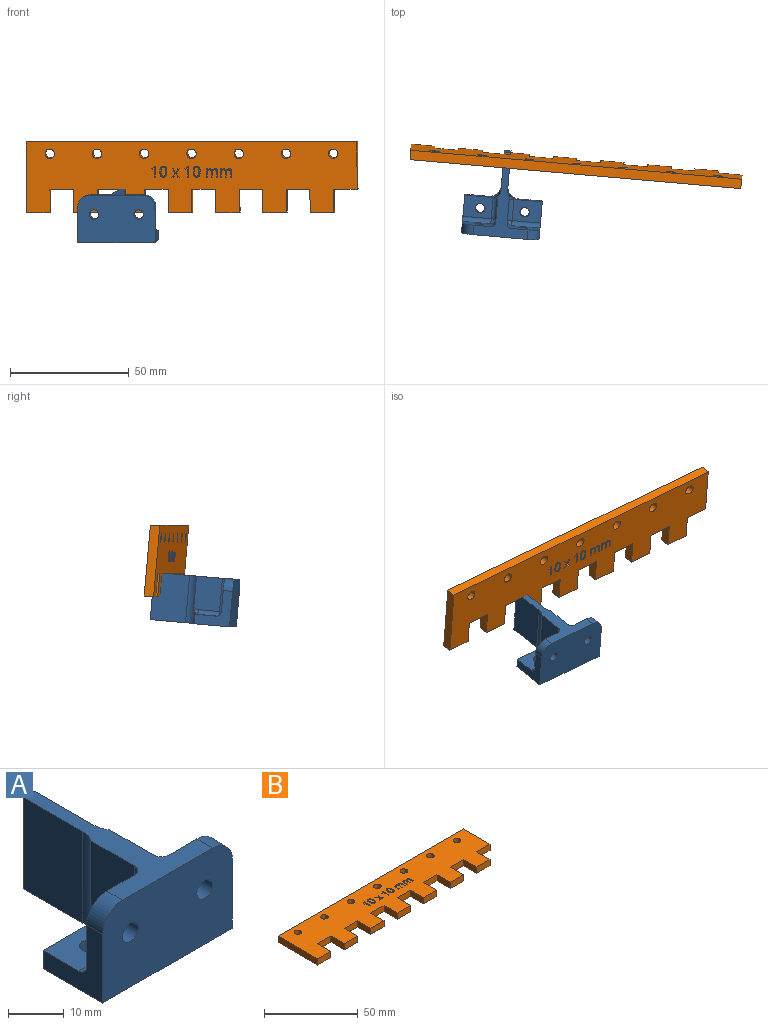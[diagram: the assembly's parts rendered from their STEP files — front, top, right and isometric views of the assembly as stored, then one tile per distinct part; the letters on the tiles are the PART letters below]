
ASSEMBLY  parts=2 mates=3
PART A: 36 faces, bbox 32.8x35x20 mm
  f0: plane 32.8x20mm, normal (0,-1,0), area 620.1mm2, adj f1,f10,f12,f13,f24,f25,f26,f27
  f1: plane 15x15mm, normal (1,0,0), area 104.9mm2, adj f0,f2,f13,f14,f15,f16,f27
  f2: plane 10x4mm, normal (0,1,0), area 40mm2, adj f1,f3,f13,f16
  f3: cylinder r=5mm len=20mm, axis (0,0,-1), area 84.6mm2, adj f2,f4,f12,f13,f17,f18,f28
  f4: plane 20x15mm, normal (1,0,0), area 300mm2, adj f3,f5,f12,f13
  f5: plane 20x2.8mm, normal (0,1,0), area 56mm2, adj f4,f6,f12,f13
  f6: plane 20x15mm, normal (-1,0,0), area 300mm2, adj f5,f7,f12,f13
  f7: cylinder r=5mm len=20mm, axis (0,0,-1), area 84.6mm2, adj f6,f8,f12,f13,f21,f23,f35
  f8: plane 10x4mm, normal (0,1,0), area 40mm2, adj f7,f10,f13,f22
  f9: cylinder r=2mm len=4mm, axis (0,0,-1), area 50.3mm2, adj f13,f22
  f10: plane 15x15mm, normal (-1,0,0), area 104.9mm2, adj f0,f8,f13,f19,f20,f22,f26
  f11: cylinder r=2mm len=4mm, axis (0,0,-1), area 50.3mm2, adj f13,f16
  f12: plane 35x22.8mm, normal (0,0,1), area 207.6mm2, adj f0,f3,f4,f5,f6,f7,f14,f18
  f13: plane 35x32.8mm, normal (0,0,-1), area 533.6mm2, adj f0,f1,f2,f3,f4,f5,f6,f7
  f14: plane 14x12mm, normal (0,1,0), area 150.1mm2, adj f1,f12,f15,f25,f27,f29
  f15: cylinder r=2mm len=12mm, axis (1,0,0), area 37.7mm2, adj f1,f14,f16,f31
  f16: plane 12x9mm, normal (0,0,1), area 95.4mm2, adj f1,f2,f11,f15,f17,f30
  f17: cylinder r=5mm len=2mm, axis (1,0,0), area 0.3mm2, adj f3,f16,f28
  f18: plane 14x11mm, normal (1,0,0), area 153.5mm2, adj f3,f12,f28,f29,f30
  f19: cylinder r=2mm len=12mm, axis (-1,0,0), area 37.7mm2, adj f10,f20,f22,f33
  f20: plane 14x12mm, normal (0,1,0), area 150.1mm2, adj f10,f12,f19,f24,f26,f32
  f21: cylinder r=5mm len=2mm, axis (-1,0,0), area 0.3mm2, adj f7,f22,f35
  f22: plane 12x9mm, normal (0,0,1), area 95.4mm2, adj f8,f9,f10,f19,f21,f34
  f23: plane 14x11mm, normal (-1,0,0), area 153.5mm2, adj f7,f12,f32,f34,f35
  f24: cylinder r=2mm len=4mm, axis (0,-1,0), area 50.3mm2, adj f0,f20
  f25: cylinder r=2mm len=4mm, axis (0,-1,0), area 50.3mm2, adj f0,f14
  f26: cylinder r=5mm len=5mm, axis (0,1,0), area 31.4mm2, adj f0,f10,f12,f20
  f27: cylinder r=5mm len=5mm, axis (0,-1,0), area 31.4mm2, adj f0,f1,f12,f14
  f28: torus R=3mm, axis (1,0,0), area 4.3mm2, adj f3,f17,f18,f30
  f29: cylinder r=2mm len=14mm, axis (0,0,-1), area 44mm2, adj f12,f14,f18,f31
  f30: cylinder r=2mm len=9mm, axis (0,1,0), area 28.3mm2, adj f16,f18,f28,f31
  f31: sphere r=2mm, area 6.3mm2, adj f15,f29,f30
  f32: cylinder r=2mm len=14mm, axis (0,0,1), area 44mm2, adj f12,f20,f23,f33
  f33: sphere r=2mm, area 6.3mm2, adj f19,f32,f34
  f34: cylinder r=2mm len=9mm, axis (0,-1,0), area 28.3mm2, adj f22,f23,f33,f35
  f35: torus R=3mm, axis (-1,0,0), area 4.3mm2, adj f7,f21,f23,f34
PART B: 166 faces, bbox 140x30x4 mm
  f0: plane 140x30mm, normal (0,0,1), area 3365.2mm2, adj f1,f2,f3,f4,f5,f6,f7,f8
  f1: plane 10x4mm, normal (-1,0,0), area 40mm2, adj f0,f2,f30,f31
  f2: plane 10x4mm, normal (0,-1,0), area 40mm2, adj f0,f1,f3,f31
  f3: plane 10x4mm, normal (1,0,0), area 40mm2, adj f0,f2,f4,f31
  f4: plane 10x4mm, normal (0,-1,0), area 40mm2, adj f0,f3,f5,f31
  f5: plane 10x4mm, normal (-1,0,0), area 40mm2, adj f0,f4,f6,f31
  f6: plane 10x4mm, normal (0,-1,0), area 40mm2, adj f0,f5,f7,f31
  f7: plane 10x4mm, normal (1,0,0), area 40mm2, adj f0,f6,f8,f31
  f8: plane 10x4mm, normal (0,-1,0), area 40mm2, adj f0,f7,f9,f31
  f9: plane 10x4mm, normal (-1,0,0), area 40mm2, adj f0,f8,f10,f31
  f10: plane 10x4mm, normal (0,-1,0), area 40mm2, adj f0,f9,f11,f31
  f11: plane 10x4mm, normal (1,0,0), area 40mm2, adj f0,f10,f12,f31
  f12: plane 10x4mm, normal (0,-1,0), area 40mm2, adj f0,f11,f13,f31
  f13: plane 10x4mm, normal (-1,0,0), area 40mm2, adj f0,f12,f14,f31
  f14: plane 10x4mm, normal (0,-1,0), area 40mm2, adj f0,f13,f15,f31
  f15: plane 10x4mm, normal (1,0,0), area 40mm2, adj f0,f14,f16,f31
  f16: plane 10x4mm, normal (0,-1,0), area 40mm2, adj f0,f15,f17,f31
  f17: plane 20x4mm, normal (1,0,0), area 80mm2, adj f0,f16,f18,f31
  f18: plane 140x4mm, normal (0,1,0), area 560mm2, adj f0,f17,f19,f31
  f19: plane 30x4mm, normal (-1,0,0), area 120mm2, adj f0,f18,f20,f31
  f20: plane 10x4mm, normal (0,-1,0), area 40mm2, adj f0,f19,f21,f31
  f21: plane 10x4mm, normal (1,0,0), area 40mm2, adj f0,f20,f22,f31
  f22: plane 10x4mm, normal (0,-1,0), area 40mm2, adj f0,f21,f23,f31
  f23: plane 10x4mm, normal (-1,0,0), area 40mm2, adj f0,f22,f24,f31
  f24: plane 10x4mm, normal (0,-1,0), area 40mm2, adj f0,f23,f25,f31
  f25: plane 10x4mm, normal (1,0,0), area 40mm2, adj f0,f24,f26,f31
  f26: plane 10x4mm, normal (0,-1,0), area 40mm2, adj f0,f25,f27,f31
  f27: plane 10x4mm, normal (-1,0,0), area 40mm2, adj f0,f26,f28,f31
  f28: plane 10x4mm, normal (0,-1,0), area 40mm2, adj f0,f27,f29,f31
  f29: plane 10x4mm, normal (1,0,0), area 40mm2, adj f0,f28,f30,f31
  f30: plane 10x4mm, normal (0,-1,0), area 40mm2, adj f0,f1,f29,f31
  f31: plane 140x30mm, normal (0,0,-1), area 3412mm2, adj f1,f2,f3,f4,f5,f6,f7,f8
  f32: cylinder r=2mm len=4mm, axis (0,0,1), area 50.3mm2, adj f0,f31
  f33: cylinder r=2mm len=4mm, axis (0,0,1), area 50.3mm2, adj f0,f31
  f34: cylinder r=2mm len=4mm, axis (0,0,1), area 50.3mm2, adj f0,f31
  f35: cylinder r=2mm len=4mm, axis (0,0,1), area 50.3mm2, adj f0,f31
  f36: cylinder r=2mm len=4mm, axis (0,0,1), area 50.3mm2, adj f0,f31
  f37: cylinder r=2mm len=4mm, axis (0,0,1), area 50.3mm2, adj f0,f31
  f38: cylinder r=2mm len=4mm, axis (0,0,1), area 50.3mm2, adj f0,f31
  f39: plane 2x1.68mm, normal (0.81,0.58,0), area 4.1mm2, adj f0,f40,f50,f51
  f40: plane 2x1.76mm, normal (0.81,-0.58,0), area 4.3mm2, adj f0,f39,f41,f51
  f41: plane 2x0.59mm, normal (0,1,0), area 1.2mm2, adj f0,f40,f42,f51
  f42: plane 2x1.4mm, normal (-0.82,0.57,0), area 3.4mm2, adj f0,f41,f43,f51
  f43: plane 2x1.4mm, normal (0.82,0.57,0), area 3.4mm2, adj f0,f42,f44,f51
  f44: plane 2x0.59mm, normal (0,1,0), area 1.2mm2, adj f0,f43,f45,f51
  f45: plane 2x1.76mm, normal (-0.81,-0.58,0), area 4.3mm2, adj f0,f44,f46,f51
  f46: plane 2x1.68mm, normal (-0.81,0.58,0), area 4.1mm2, adj f0,f45,f47,f51
  f47: plane 2x0.59mm, normal (0,-1,0), area 1.2mm2, adj f0,f46,f48,f51
  f48: plane 2x1.32mm, normal (0.82,-0.57,0), area 3.2mm2, adj f0,f47,f49,f51
  f49: plane 2x1.32mm, normal (-0.82,-0.57,0), area 3.2mm2, adj f0,f48,f50,f51
  f50: plane 2x0.59mm, normal (0,-1,0), area 1.2mm2, adj f0,f39,f49,f51
  f51: plane 3.44x3.12mm, normal (0,0,1), area 3.7mm2, adj f39,f40,f41,f42,f43,f44,f45,f46
  f52: plane 2x0.51mm, normal (0,1,0), area 1mm2, adj f0,f53,f60,f61
  f53: plane 4.59x2mm, normal (-1,0,0), area 9.2mm2, adj f0,f52,f54,f61
  f54: plane 2x0.44mm, normal (0,-1,0), area 0.9mm2, adj f0,f53,f55,f61
  f55: plane 2x1.22mm, normal (0.61,-0.79,0), area 3.1mm2, adj f0,f54,f56,f61
  f56: plane 2x0.36mm, normal (0.79,0.61,0), area 0.9mm2, adj f0,f55,f57,f61
  f57: extruded ~2x0.75mm, area 1.9mm2, adj f0,f56,f58,f61
  f58: extruded ~2x0.15mm, area 0.4mm2, adj f0,f57,f59,f61
  f59: extruded ~2x0.77mm, area 1.5mm2, adj f0,f58,f60,f61
  f60: plane 3.27x2mm, normal (1,0,0), area 6.5mm2, adj f0,f52,f59,f61
  f61: plane 4.59x1.65mm, normal (0,0,1), area 2.9mm2, adj f52,f53,f54,f55,f56,f57,f58,f59
  f62: plane 2.24x2mm, normal (1,0,0), area 4.5mm2, adj f0,f63,f89,f90
  f63: plane 2x0.52mm, normal (0,1,0), area 1mm2, adj f0,f62,f64,f90
  f64: plane 2.25x2mm, normal (-1,0,0), area 4.5mm2, adj f0,f63,f65,f90
  f65: extruded ~2x0.96mm, area 2.1mm2, adj f0,f64,f66,f90
  f66: extruded ~2x0.87mm, area 1.9mm2, adj f0,f65,f67,f90
  f67: extruded ~2x0.67mm, area 1.4mm2, adj f0,f66,f68,f90
  f68: extruded ~2x0.45mm, area 1.3mm2, adj f0,f67,f69,f90
  f69: plane 2x0.03mm, normal (0,-1,0), area 0.1mm2, adj f0,f68,f70,f90
  f70: extruded ~2x1.06mm, area 2.6mm2, adj f0,f69,f71,f90
  f71: extruded ~2x0.6mm, area 1.2mm2, adj f0,f70,f72,f90
  f72: extruded ~2x0.42mm, area 1.2mm2, adj f0,f71,f73,f90
  f73: plane 2x0.03mm, normal (0,-1,0), area 0.1mm2, adj f0,f72,f74,f90
  f74: plane 2x0.47mm, normal (-0.98,-0.18,0), area 1mm2, adj f0,f73,f75,f90
  f75: plane 2x0.42mm, normal (0,-1,0), area 0.8mm2, adj f0,f74,f76,f90
  f76: plane 3.44x2mm, normal (1,0,0), area 6.9mm2, adj f0,f75,f77,f90
  f77: plane 2x0.52mm, normal (0,1,0), area 1mm2, adj f0,f76,f78,f90
  f78: plane 2x1.81mm, normal (-1,0,0), area 3.6mm2, adj f0,f77,f79,f90
  f79: extruded ~2x0.96mm, area 2mm2, adj f0,f78,f80,f90
  f80: extruded ~2x0.72mm, area 1.6mm2, adj f0,f79,f81,f90
  f81: extruded ~2x0.55mm, area 1.2mm2, adj f0,f80,f82,f90
  f82: extruded ~2x0.62mm, area 1.3mm2, adj f0,f81,f83,f90
  f83: plane 2.24x2mm, normal (1,0,0), area 4.5mm2, adj f0,f82,f84,f90
  f84: plane 2x0.52mm, normal (0,1,0), area 1mm2, adj f0,f83,f85,f90
  f85: plane 2x1.92mm, normal (-1,0,0), area 3.8mm2, adj f0,f84,f86,f90
  f86: extruded ~2x0.86mm, area 1.8mm2, adj f0,f85,f87,f90
  f87: extruded ~2x0.72mm, area 1.6mm2, adj f0,f86,f88,f90
  f88: extruded ~2x0.55mm, area 1.2mm2, adj f0,f87,f89,f90
  f89: extruded ~2x0.62mm, area 1.3mm2, adj f0,f62,f88,f90
  f90: plane 4.91x3.51mm, normal (0,0,1), area 6.7mm2, adj f62,f63,f64,f65,f66,f67,f68,f69
  f91: plane 2.24x2mm, normal (1,0,0), area 4.5mm2, adj f0,f92,f118,f119
  f92: plane 2x0.52mm, normal (0,1,0), area 1mm2, adj f0,f91,f93,f119
  f93: plane 2.25x2mm, normal (-1,0,0), area 4.5mm2, adj f0,f92,f94,f119
  f94: extruded ~2x0.96mm, area 2.1mm2, adj f0,f93,f95,f119
  f95: extruded ~2x0.87mm, area 1.9mm2, adj f0,f94,f96,f119
  f96: extruded ~2x0.67mm, area 1.4mm2, adj f0,f95,f97,f119
  f97: extruded ~2x0.45mm, area 1.3mm2, adj f0,f96,f98,f119
  f98: plane 2x0.03mm, normal (0,-1,0), area 0.1mm2, adj f0,f97,f99,f119
  f99: extruded ~2x1.06mm, area 2.6mm2, adj f0,f98,f100,f119
  f100: extruded ~2x0.6mm, area 1.2mm2, adj f0,f99,f101,f119
  f101: extruded ~2x0.42mm, area 1.2mm2, adj f0,f100,f102,f119
  f102: plane 2x0.03mm, normal (0,-1,0), area 0.1mm2, adj f0,f101,f103,f119
  f103: plane 2x0.47mm, normal (-0.98,-0.18,0), area 1mm2, adj f0,f102,f104,f119
  f104: plane 2x0.42mm, normal (0,-1,0), area 0.8mm2, adj f0,f103,f105,f119
  f105: plane 3.44x2mm, normal (1,0,0), area 6.9mm2, adj f0,f104,f106,f119
  f106: plane 2x0.52mm, normal (0,1,0), area 1mm2, adj f0,f105,f107,f119
  f107: plane 2x1.81mm, normal (-1,0,0), area 3.6mm2, adj f0,f106,f108,f119
  f108: extruded ~2x0.96mm, area 2mm2, adj f0,f107,f109,f119
  f109: extruded ~2x0.72mm, area 1.6mm2, adj f0,f108,f110,f119
  f110: extruded ~2x0.55mm, area 1.2mm2, adj f0,f109,f111,f119
  f111: extruded ~2x0.62mm, area 1.3mm2, adj f0,f110,f112,f119
  f112: plane 2.24x2mm, normal (1,0,0), area 4.5mm2, adj f0,f111,f113,f119
  f113: plane 2x0.52mm, normal (0,1,0), area 1mm2, adj f0,f112,f114,f119
  f114: plane 2x1.92mm, normal (-1,0,0), area 3.8mm2, adj f0,f113,f115,f119
  f115: extruded ~2x0.86mm, area 1.8mm2, adj f0,f114,f116,f119
  f116: extruded ~2x0.72mm, area 1.6mm2, adj f0,f115,f117,f119
  f117: extruded ~2x0.55mm, area 1.2mm2, adj f0,f116,f118,f119
  f118: extruded ~2x0.62mm, area 1.3mm2, adj f0,f91,f117,f119
  f119: plane 4.91x3.51mm, normal (0,0,1), area 6.7mm2, adj f91,f92,f93,f94,f95,f96,f97,f98
  f120: extruded ~2x1.46mm, area 3mm2, adj f121,f135,f136,f164
  f121: extruded ~2x1.46mm, area 3mm2, adj f120,f122,f136,f164
  f122: extruded ~2x0.75mm, area 1.9mm2, adj f121,f123,f136,f164
  f123: extruded ~2x0.76mm, area 1.9mm2, adj f122,f124,f136,f164
  f124: extruded ~2x1.45mm, area 3mm2, adj f123,f125,f136,f164
  f125: extruded ~2x1.45mm, area 3mm2, adj f124,f126,f136,f164
  f126: extruded ~2x0.76mm, area 1.9mm2, adj f125,f135,f136,f164
  f127: extruded ~2x1.78mm, area 3.7mm2, adj f0,f128,f134,f136
  f128: extruded ~2x1.76mm, area 3.6mm2, adj f0,f127,f129,f136
  f129: extruded ~2x1.14mm, area 2.7mm2, adj f0,f128,f130,f136
  f130: extruded ~2x1.14mm, area 2.7mm2, adj f0,f129,f131,f136
  f131: extruded ~2x1.78mm, area 3.7mm2, adj f0,f130,f132,f136
  f132: extruded ~2x1.76mm, area 3.7mm2, adj f0,f131,f133,f136
  f133: extruded ~2x1.13mm, area 2.7mm2, adj f0,f132,f134,f136
  f134: extruded ~2x1.15mm, area 2.7mm2, adj f0,f127,f133,f136
  f135: extruded ~2x0.75mm, area 1.9mm2, adj f120,f126,f136,f164
  f136: plane 4.73x3.04mm, normal (0,0,1), area 5.6mm2, adj f120,f121,f122,f123,f124,f125,f126,f127
  f137: extruded ~2x1.46mm, area 3mm2, adj f138,f152,f153,f165
  f138: extruded ~2x1.46mm, area 3mm2, adj f137,f139,f153,f165
  f139: extruded ~2x0.75mm, area 1.9mm2, adj f138,f140,f153,f165
  f140: extruded ~2x0.76mm, area 1.9mm2, adj f139,f141,f153,f165
  f141: extruded ~2x1.45mm, area 3mm2, adj f140,f142,f153,f165
  f142: extruded ~2x1.45mm, area 3mm2, adj f141,f143,f153,f165
  f143: extruded ~2x0.76mm, area 1.9mm2, adj f142,f152,f153,f165
  f144: extruded ~2x1.78mm, area 3.7mm2, adj f0,f145,f151,f153
  f145: extruded ~2x1.76mm, area 3.6mm2, adj f0,f144,f146,f153
  f146: extruded ~2x1.14mm, area 2.7mm2, adj f0,f145,f147,f153
  f147: extruded ~2x1.14mm, area 2.7mm2, adj f0,f146,f148,f153
  f148: extruded ~2x1.78mm, area 3.7mm2, adj f0,f147,f149,f153
  f149: extruded ~2x1.76mm, area 3.7mm2, adj f0,f148,f150,f153
  f150: extruded ~2x1.13mm, area 2.7mm2, adj f0,f149,f151,f153
  f151: extruded ~2x1.15mm, area 2.7mm2, adj f0,f144,f150,f153
  f152: extruded ~2x0.75mm, area 1.9mm2, adj f137,f143,f153,f165
  f153: plane 4.73x3.04mm, normal (0,0,1), area 5.6mm2, adj f137,f138,f139,f140,f141,f142,f143,f144
  f154: plane 2x0.51mm, normal (0,1,0), area 1mm2, adj f0,f155,f162,f163
  f155: plane 4.59x2mm, normal (-1,0,0), area 9.2mm2, adj f0,f154,f156,f163
  f156: plane 2x0.44mm, normal (0,-1,0), area 0.9mm2, adj f0,f155,f157,f163
  f157: plane 2x1.22mm, normal (0.61,-0.79,0), area 3.1mm2, adj f0,f156,f158,f163
  f158: plane 2x0.36mm, normal (0.79,0.61,0), area 0.9mm2, adj f0,f157,f159,f163
  f159: extruded ~2x0.75mm, area 1.9mm2, adj f0,f158,f160,f163
  f160: extruded ~2x0.15mm, area 0.4mm2, adj f0,f159,f161,f163
  f161: extruded ~2x0.77mm, area 1.5mm2, adj f0,f160,f162,f163
  f162: plane 3.27x2mm, normal (1,0,0), area 6.5mm2, adj f0,f154,f161,f163
  f163: plane 4.59x1.65mm, normal (0,0,1), area 2.9mm2, adj f154,f155,f156,f157,f158,f159,f160,f161
  f164: plane 3.83x1.98mm, normal (0,0,1), area 6.4mm2, adj f120,f121,f122,f123,f124,f125,f126,f135
  f165: plane 3.83x1.98mm, normal (0,0,1), area 6.4mm2, adj f137,f138,f139,f140,f141,f142,f143,f152
PLACE A rot(axis=(0.71,-0.03,-0.71),7.1deg) t=(-38.66,-15.07,12.19)mm
PLACE B rot(axis=(1,-0.04,-0.04),95.1deg) t=(-77.96,-13.38,32.12)mm
MATE parallel A.f10 <-> B.f19  axis (-1,0.09,0) through (-56.23,-43.82,14.74)mm
MATE parallel B.f18 <-> A.f12  axis (-0.01,-0.09,1) through (-8.56,-23.2,51.87)mm
MATE planar A.f12 <-> B.f4  axis (-0.01,-0.09,1) through (-37.42,-16.93,32.12)mm
